# Revit family: Shower-Showerhead_Kit-KALLISTA-PER_SE-P24712_1
name_source: partatom
category: Plumbing Fixtures
units: mm (PartAtom-declared; Revit-internal decimal feet)

## family parameters
Cut with Voids When Loaded = No
Host = Face
Maintain Annotation Orientation = No
OmniClass Number = 23.31.17.00
OmniClass Title = Showers
Part Type = Normal
Room Calculation Point = No
Round Connector Dimension = Use Diameter
Shared = No

## types (5) — shared parameters
ADA Compliant = No
Assembly Code = D2010700
CW Connection = No
Cold Water Inlet = Cold Water Inlet
Date Modified = 03/29/2022
Default Elevation = 72"
Description = AIR-INDUCTION SHOWERHEAD WITH ARM
Drain Included = No
Flow Rate = 2 GPM
HW Connection = Yes
Height = 6 5/16"
Hot Water Inlet = Hot Water Inlet
Length = 8"
Manufacturer = KALLISTA Co.
Master Format 2014 = 22 42 23
Master Format 2014 Name = Residential Showers
Material = Premium Metal Construction
Panel Thickness = 0"
Pressure = 80.00 psi
Product Name = PER SE
Product Page URL = https://www.kallista.com
Tempered Water Inlet = Tempered Water Inlet
URL = https://www.kallista.com
Vent Connection = No
Waste Connection = No
Waste Water Outlet = Waste Water Outlet
WaterSense Certified = Yes
Width = 4 1/4"

## per-type parameters (varying)
| type | Finish | Model | Type |
| AF-French Gold | Kallista-Metal-AF-French_Gold | P24712-00-AF | 1 |
| BAF-Brushed French Gold | Kallista-Metal-BAF-Brushed_French_Gold | P24712-00-BAF | 2 |
| BN-Brushed Nickel | Kallista-Metal-BN-Brushed_Nickel | P24712-00-BN | 3 |
| CP-Chrome | Kallista-Metal-CP-Chrome | P24712-00-CP | 4 |
| SN-Polished Nickel | Kallista-Metal-SN-Polished_Nickel | P24712-00-SN | 5 |

## geometry (parser evidence)
native form markers: Sweep x5
no freeform markers — native parametric forms only
